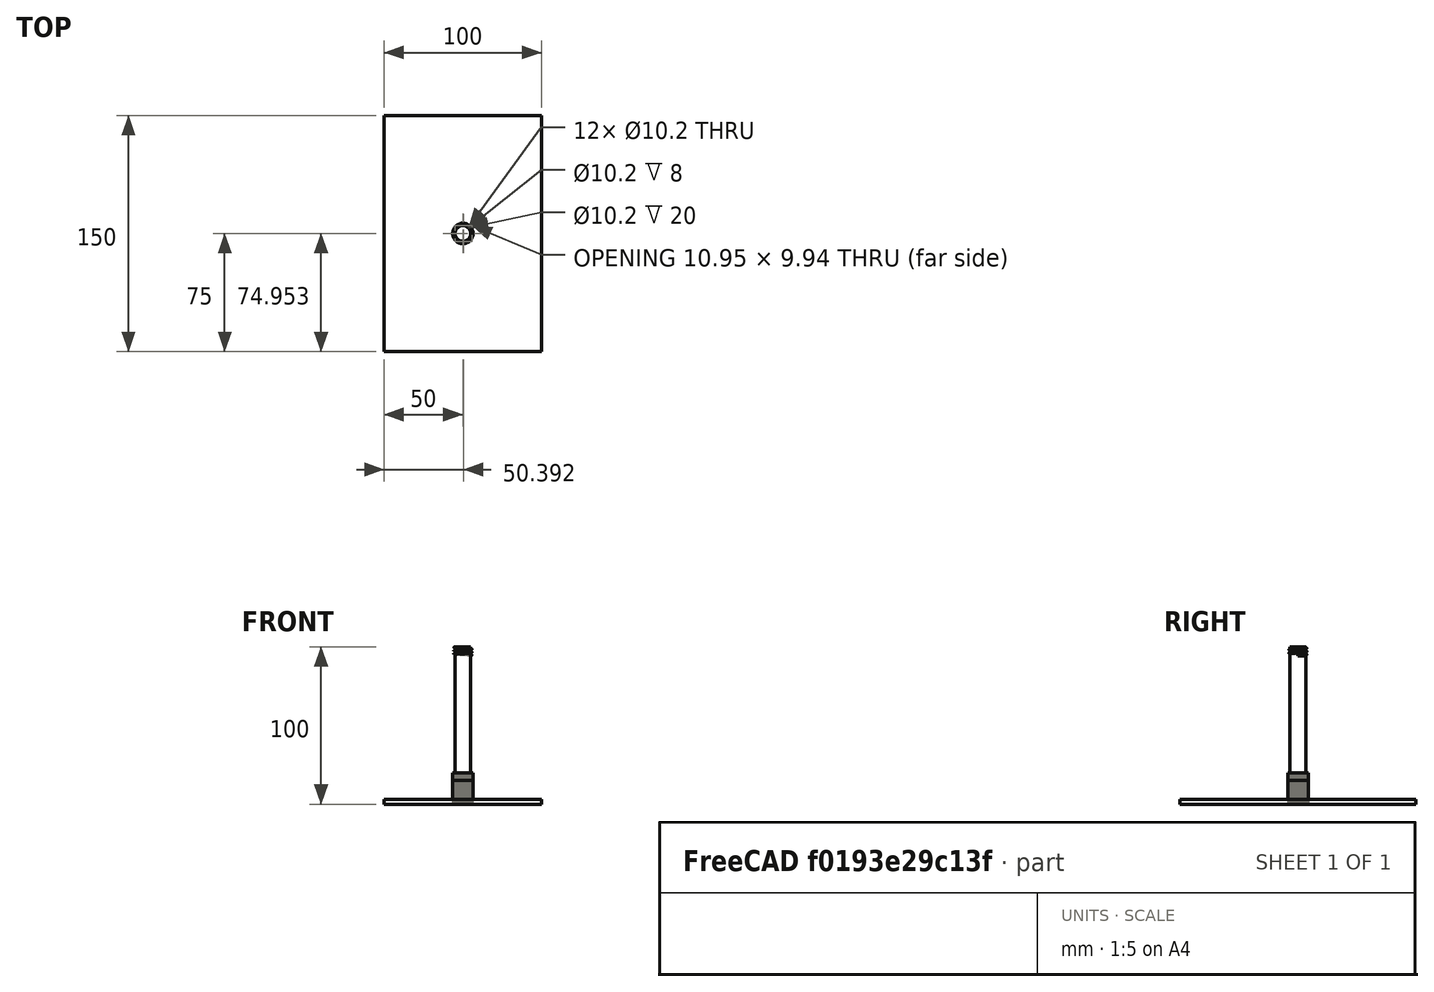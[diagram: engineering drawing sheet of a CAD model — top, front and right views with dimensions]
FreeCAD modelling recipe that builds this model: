
FCSTD DOCUMENT  (FreeCAD 0.17R13519 (Git))
Label: FengQiangZhiJia-jwei-1.0
License: All rights reserved
LicenseURL: http://en.wikipedia.org/wiki/All_rights_reserved
objects: Sketcher::SketchObject×10, PartDesign::Pad×4, Part::Helix×4, Part::Sweep×4, PartDesign::Body×3, PartDesign::Pocket×2, Part::Cut×2, PartDesign::FeatureBase×1, Part::MultiFuse×1, Part::Fuse×1
note: 38 computed .brp shape members not serialized (recipe doc carries the construction recipe); baked Part::Feature solids carry a one-line shape summary decoded from their .brp

FEATURE [Sketcher::SketchObject] Sketch
  MapMode = 5
  Support = -> [XY_Plane]
  sketch-geometry (4):
    g0: LineSegment StartX=-50 StartY=75 StartZ=0 EndX=50 EndY=75 EndZ=0
    g1: LineSegment StartX=50 StartY=75 StartZ=0 EndX=50 EndY=-75 EndZ=0
    g2: LineSegment StartX=50 StartY=-75 StartZ=0 EndX=-50 EndY=-75 EndZ=0
    g3: LineSegment StartX=-50 StartY=-75 StartZ=0 EndX=-50 EndY=75 EndZ=0
  constraints (12):
    c: Coincident(g0,g1)
    c: Coincident(g1,g2)
    c: Coincident(g2,g3)
    c: Coincident(g3,g0)
    c: Horizontal(g0)
    c: Horizontal(g2)
    c: Vertical(g1)
    c: Vertical(g3)
    c: DistanceX(g0,g0) = 100
    c: DistanceY(g3,g3) = 150
    c: Distance(g-1,g0) = 75
    c: Distance(g-1,g3) = 50
FEATURE [PartDesign::Pad] Pad
  Length = 3
  Length2 = 100
  Profile = -> Sketch
  Type = 0
FEATURE [Sketcher::SketchObject] Sketch001
  MapMode = 5
  Placement = pos=(0,0,3) rot=(0,0,1;0rad)
  Support = -> [Pad]
  sketch-geometry (1):
    g0: Circle CenterX=0 CenterY=0 CenterZ=0 NormalX=0 NormalY=0 NormalZ=1 AngleXU=0 Radius=6.5
  constraints (2):
    c: Radius(g0) = 6.5
    c: Coincident(g0,g-1)
FEATURE [PartDesign::Pad] Pad001
  BaseFeature = -> Pad
  Length = 12
  Length2 = 100
  Profile = -> Sketch001
  Type = 0
FEATURE [Sketcher::SketchObject] Sketch002
  MapMode = 5
  Placement = pos=(0,0,15) rot=(0,0,1;0rad)
  Support = -> [Pad001]
  sketch-geometry (1):
    g0: Circle CenterX=0 CenterY=0 CenterZ=0 NormalX=0 NormalY=0 NormalZ=1 AngleXU=0 Radius=5.1
  constraints (2):
    c: Radius(g0) = 5.1
    c: Coincident(g0,g-1)
FEATURE [PartDesign::Pocket] Pocket
  BaseFeature = -> Pad001
  Length = 8
  Length2 = 100
  Profile = -> Sketch002
  Type = 0
FEATURE [Sketcher::SketchObject] Sketch003
  MapMode = 5
  Placement = pos=(0,0,0) rot=(1,0,0;1.5708rad)
  Support = -> [XZ_Plane]
  sketch-geometry (3):
    g0: LineSegment StartX=5 StartY=0.5 StartZ=0 EndX=5 EndY=-0.5 EndZ=0
    g1: LineSegment StartX=5 StartY=-0.5 StartZ=0 EndX=5.86603 EndY=0 EndZ=0
    g2: LineSegment StartX=5.86603 StartY=0 StartZ=0 EndX=5 EndY=0.5 EndZ=0
  constraints (9):
    c: Coincident(g0,g1)
    c: Coincident(g1,g2)
    c: Coincident(g2,g0)
    c: DistanceY(g0,g0) = 1
    c: Angle(g0,g2) = 1.0472
    c: Angle(g1,g0) = 1.0472
    c: Vertical(g0)
    c: PointOnObject(g1,g-1)
    c: Distance(g-1,g0) = 5
FEATURE [PartDesign::Body] Body  label="main1"
  Group = -> [Sketch,Pad,Sketch001,Pad001,Sketch002,Pocket,Sketch003]
  Origin = -> Origin
  Tip = -> Pocket
FEATURE [Part::Helix] Helix  label="螺旋体1"
  Angle = 0
  AttacherType = Attacher::AttachEngine3D
  Height = 8
  LocalCoord = 0
  Pitch = 2
  Radius = 5
  Style = 1
FEATURE [Part::Sweep] Sweep
  Frenet = true
  Placement = pos=(0,0,7) rot=(0,0,1;0rad)
  Sections = -> [Sketch003]
  Solid = true
  Spine = -> Helix
  Transition = 1
FEATURE [Part::Cut] Cut  label="1"
  Base = -> Pocket
  Tool = -> Sweep
FEATURE [Sketcher::SketchObject] Sketch004
  MapMode = 5
  Support = -> [XY_Plane001]
  sketch-geometry (1):
    g0: Circle CenterX=0 CenterY=0 CenterZ=0 NormalX=0 NormalY=0 NormalZ=1 AngleXU=0 Radius=6.5
  constraints (2):
    c: Radius(g0) = 6.5
    c: Coincident(g0,g-1)
FEATURE [PartDesign::FeatureBase] BaseFeature
  BaseFeature = -> Helix
FEATURE [PartDesign::Pad] Pad002
  BaseFeature = -> BaseFeature
  Length = 20
  Length2 = 100
  Profile = -> Sketch004
  Type = 0
FEATURE [Part::Helix] Helix001  label="螺旋体2"
  Angle = 0
  AttacherType = Attacher::AttachEngine3D
  Height = 20
  LocalCoord = 0
  Pitch = 2
  Radius = 5
  Style = 1
FEATURE [Sketcher::SketchObject] Sketch005
  MapMode = 5
  Placement = pos=(0,0,20) rot=(0,0,1;0rad)
  Support = -> [Pad002]
  sketch-geometry (1):
    g0: Circle CenterX=0 CenterY=0 CenterZ=0 NormalX=0 NormalY=0 NormalZ=1 AngleXU=0 Radius=5.1
  constraints (2):
    c: Radius(g0) = 5.1
    c: Coincident(g0,g-1)
FEATURE [PartDesign::Pocket] Pocket001
  BaseFeature = -> Pad002
  Length = 5
  Length2 = 100
  Profile = -> Sketch005
  Type = 1
FEATURE [Sketcher::SketchObject] Sketch006
  MapMode = 5
  Placement = pos=(0,0,0) rot=(1,0,0;1.5708rad)
  Support = -> [XZ_Plane001]
  sketch-geometry (3):
    g0: LineSegment StartX=5 StartY=0.5 StartZ=0 EndX=5 EndY=-0.5 EndZ=0
    g1: LineSegment StartX=5 StartY=-0.5 StartZ=0 EndX=5.86603 EndY=0 EndZ=0
    g2: LineSegment StartX=5.86603 StartY=0 StartZ=0 EndX=5 EndY=0.5 EndZ=0
  constraints (9):
    c: Coincident(g0,g1)
    c: Coincident(g1,g2)
    c: Vertical(g0)
    c: DistanceY(g0,g0) = 1
    c: Coincident(g2,g0)
    c: Angle(g1,g0) = 1.0472
    c: Angle(g0,g2) = 1.0472
    c: Distance(g-1,g0) = 5
    c: PointOnObject(g1,g-1)
FEATURE [PartDesign::Body] Body001  label="main2"
  BaseFeature = -> Helix
  Group = -> [BaseFeature,Sketch004,Pad002,Sketch005,Pocket001,Sketch006]
  Origin = -> Origin001
  Tip = -> Pocket001
FEATURE [Part::Sweep] Sweep001
  Frenet = true
  Sections = -> [Sketch006]
  Solid = true
  Spine = -> Helix001
  Transition = 1
FEATURE [Part::Cut] Cut001  label="2"
  Base = -> Pocket001
  Tool = -> Sweep001
FEATURE [Part::Helix] Helix003  label="螺旋体3"
  Angle = 0
  AttacherType = Attacher::AttachEngine3D
  Height = 8
  LocalCoord = 0
  Pitch = 2
  Radius = 5
  Style = 1
FEATURE [Sketcher::SketchObject] Sketch007
  MapMode = 5
  Placement = pos=(0,0,0) rot=(1,0,0;1.5708rad)
  Support = -> [XZ_Plane002]
  sketch-geometry (3):
    g0: LineSegment StartX=5 StartY=0.5 StartZ=0 EndX=5 EndY=-0.5 EndZ=0
    g1: LineSegment StartX=5 StartY=-0.5 StartZ=0 EndX=5.86603 EndY=0 EndZ=0
    g2: LineSegment StartX=5.86603 StartY=0 StartZ=0 EndX=5 EndY=0.5 EndZ=0
  constraints (9):
    c: Coincident(g0,g1)
    c: Coincident(g1,g2)
    c: Coincident(g2,g0)
    c: DistanceY(g0,g0) = 1
    c: Angle(g1,g0) = 1.0472
    c: Angle(g0,g2) = 1.0472
    c: Vertical(g0)
    c: PointOnObject(g1,g-1)
    c: Distance(g-1,g0) = 5
FEATURE [Part::Sweep] Sweep002
  Frenet = true
  Placement = pos=(0,0,0.5) rot=(0,0,1;0rad)
  Sections = -> [Sketch007]
  Solid = true
  Spine = -> Helix003
  Transition = 1
FEATURE [Sketcher::SketchObject] Sketch008
  MapMode = 5
  Support = -> [XY_Plane002]
  sketch-geometry (1):
    g0: Circle CenterX=0 CenterY=0 CenterZ=0 NormalX=0 NormalY=0 NormalZ=1 AngleXU=0 Radius=5
  constraints (2):
    c: Radius(g0) = 5
    c: Coincident(g0,g-1)
FEATURE [PartDesign::Pad] Pad003
  Length = 100
  Length2 = 100
  Profile = -> Sketch008
  Type = 0
FEATURE [PartDesign::Body] Body002  label="main3"
  Group = -> [Sketch007,Sketch008,Pad003]
  Origin = -> Origin002
  Tip = -> Pad003
FEATURE [Sketcher::SketchObject] Sketch009
  MapMode = 5
  Placement = pos=(0,0,0) rot=(1,0,0;1.5708rad)
  Support = -> [XZ_Plane003]
  sketch-geometry (3):
    g0: LineSegment StartX=5 StartY=0.5 StartZ=0 EndX=5 EndY=-0.5 EndZ=0
    g1: LineSegment StartX=5 StartY=-0.5 StartZ=0 EndX=5.86603 EndY=0 EndZ=0
    g2: LineSegment StartX=5.86603 StartY=0 StartZ=0 EndX=5 EndY=0.5 EndZ=0
  constraints (9):
    c: Coincident(g0,g1)
    c: Coincident(g1,g2)
    c: Coincident(g2,g0)
    c: DistanceY(g0,g0) = 1
    c: Angle(g1,g0) = 1.0472
    c: Angle(g0,g2) = 1.0472
    c: Vertical(g0)
    c: PointOnObject(g1,g-1)
    c: Distance(g-1,g0) = 5
FEATURE [Part::Helix] Helix004  label="螺旋体004"
  Angle = 0
  AttacherType = Attacher::AttachEngine3D
  Height = 5
  LocalCoord = 0
  Pitch = 2
  Radius = 5
  Style = 1
FEATURE [Part::Sweep] Sweep003
  Frenet = true
  Placement = pos=(0,0,94.5) rot=(0,0,1;0rad)
  Sections = -> [Sketch009]
  Solid = true
  Spine = -> Helix004
  Transition = 1
FEATURE [Part::MultiFuse] Fusion
  Shapes = -> [Pad003,Sweep003]
FEATURE [Part::Fuse] Fusion001
  Base = -> Fusion
  Tool = -> Sweep002
